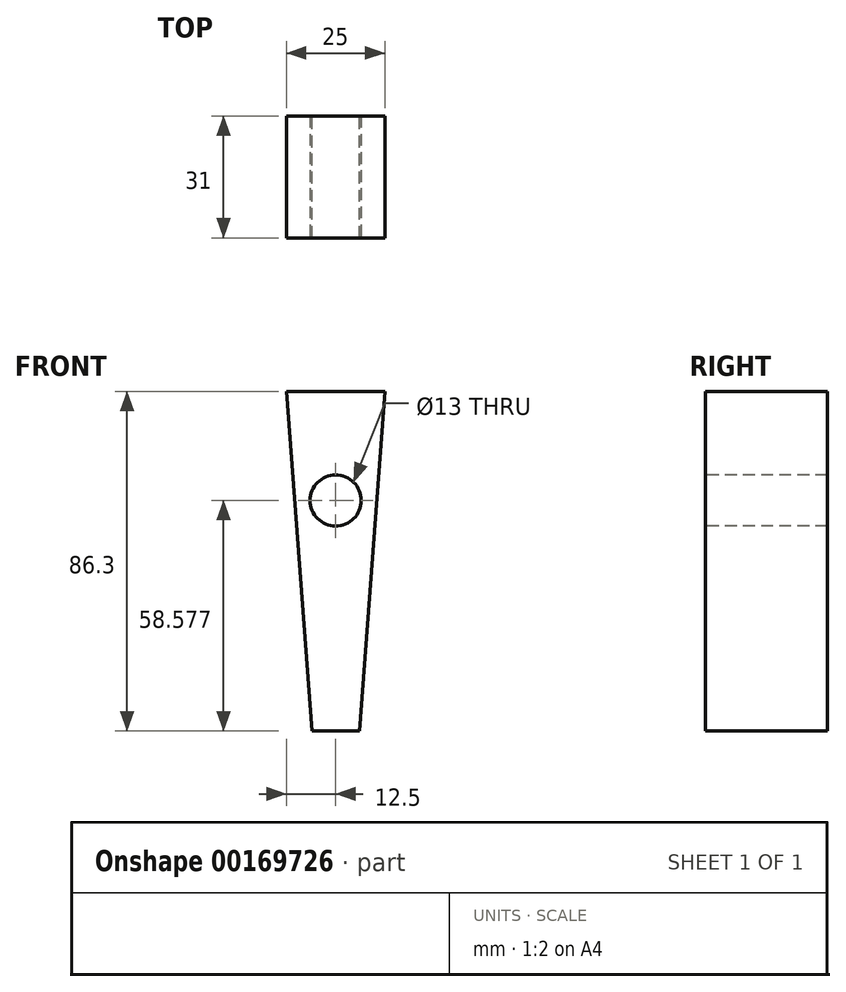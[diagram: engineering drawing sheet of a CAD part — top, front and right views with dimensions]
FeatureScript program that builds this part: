
annotation { "Feature Type Name" : "Feature", "Feature Type Description" : "" }
export const myFeature = defineFeature(function(context is Context, id is Id, definition is map)
    precondition{}
    {
        {
            var Q0;
            Q0=qCreatedBy(makeId("Top.planeOp"),FACE);
            var sketch = newSketch(context, id + "F0", { "sketchPlane" : qUnion([Q0])});
            skLineSegment(sketch, "E0.bottom", {"start": v(-12.5, 15.5) * mm, "end": v(12.5, 15.5) * mm});
            skLineSegment(sketch, "E0.top", {"start": v(-12.5, -15.5) * mm, "end": v(12.5, -15.5) * mm});
            skLineSegment(sketch, "E0.left", {"start": v(-12.5, 15.5) * mm, "end": v(-12.5, -15.5) * mm});
            skLineSegment(sketch, "E0.right", {"start": v(12.5, 15.5) * mm, "end": v(12.5, -15.5) * mm});
            skPoint(sketch, "E0.middle", {"position": v(0, 0) * mm});
            skSolve(sketch);
        }
        {
            var Q0;
            Q0=qSketchRegion(id+"F0",true);
            extrude(context, id + "F1", {"entities" : qUnion([Q0]), "depth" : 86.3 * mm});
        }
        {
            var Q0;
            Q0=qCreatedBy(makeId("Front.planeOp"),FACE);
            var sketch = newSketch(context, id + "F2", { "sketchPlane" : qUnion([Q0])});
            skCircle(sketch, "E1", {"center": v(0, 58.58) * mm, "radius": 6.5 * mm});
            skSolve(sketch);
        }
        {
            var Q0;
            Q0=qSketchRegion(id+"F2",true);
            extrude(context, id + "F3", {"entities" : qUnion([Q0]), "operationType" : NewBodyOperationType.REMOVE, "endBound" : BoundingType.SYMMETRIC, "oppositeDirection" : true, "depth" : 63 * mm});
        }
        {
            var Q0;
            Q0=makeQuery(id+"F1.opExtrude","SWEPT_FACE",FACE,{"disambiguationData":[OSD([sQuery(id+"F0.wireOp",EDGE,"E0.bottom")])]});
            var sketch = newSketch(context, id + "F4", { "sketchPlane" : qUnion([Q0])});
            skLineSegment(sketch, "E2", {"start": v(-12.5, 86.3) * mm, "end": v(-6, 0) * mm});
            skLineSegment(sketch, "E3", {"start": v(-6, 0) * mm, "end": v(6, 0) * mm});
            skLineSegment(sketch, "E4", {"start": v(6, 0) * mm, "end": v(12.5, 86.3) * mm});
            skSolve(sketch);
        }
        {
            var Q0;
            {var subQ0=sQuery(id+"F4.wireOp",EDGE,"E4");Q0=makeQuery(id+"F4.imprint","IMPRINT",FACE,{"disambiguationData":[TD([[makeQuery(id+"F4.imprint","IMPRINT",EDGE,{"derivedFrom":subQ0}),-1.0]])]});}
            var Q1;
            {var subQ0=sQuery(id+"F4.wireOp",EDGE,"E2");Q1=makeQuery(id+"F4.imprint","IMPRINT",FACE,{"disambiguationData":[TD([[makeQuery(id+"F4.imprint","IMPRINT",EDGE,{"derivedFrom":subQ0}),-1.0]])]});}
            extrude(context, id + "F5", {"entities" : qUnion([Q0, Q1]), "operationType" : NewBodyOperationType.REMOVE, "endBound" : BoundingType.THROUGH_ALL, "oppositeDirection" : true, "depth" : 25 * mm});
        }
    });
